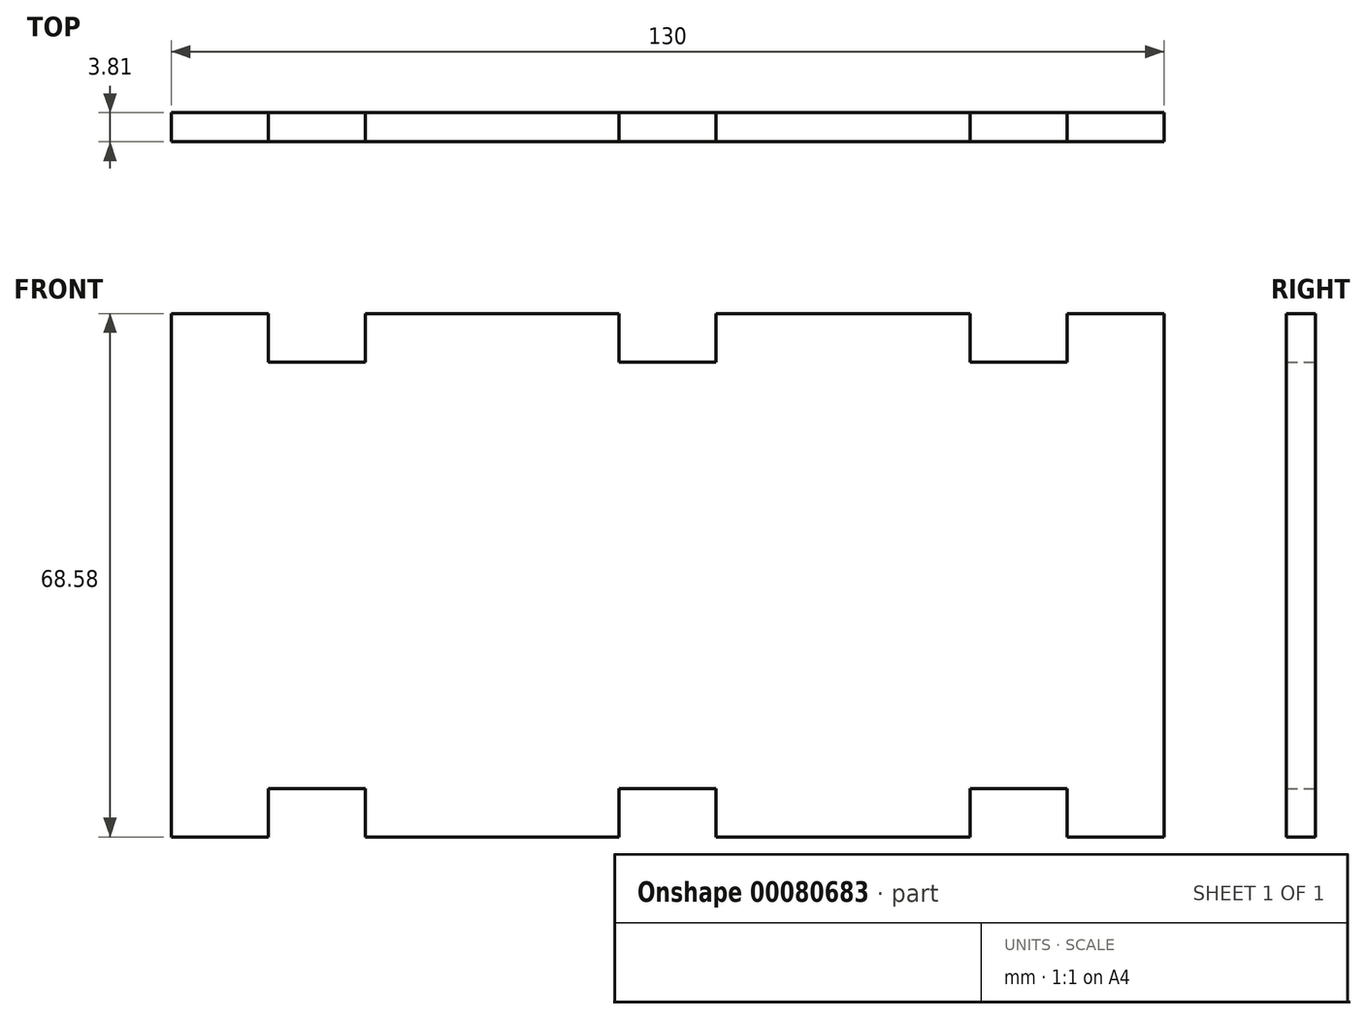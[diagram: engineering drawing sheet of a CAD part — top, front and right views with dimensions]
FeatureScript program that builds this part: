
annotation { "Feature Type Name" : "Feature", "Feature Type Description" : "" }
export const myFeature = defineFeature(function(context is Context, id is Id, definition is map)
    precondition{}
    {
        {
            var Q0;
            Q0=qCreatedBy(makeId("Front.planeOp"),FACE);
            var sketch = newSketch(context, id + "F0", { "sketchPlane" : qUnion([Q0])});
            skLineSegment(sketch, "E0.bottom", {"start": v(-65, 34.3) * mm, "end": v(-52.3, 34.3) * mm});
            skLineSegment(sketch, "E0.left", {"start": v(-65, 34.3) * mm, "end": v(-65, 0) * mm});
            skLineSegment(sketch, "E0.right", {"start": v(65, 34.3) * mm, "end": v(65, 0) * mm});
            skPoint(sketch, "E0.middle", {"position": v(0, 0) * mm});
            skLineSegment(sketch, "E1.top", {"start": v(-52.3, 27.94) * mm, "end": v(-39.6, 27.94) * mm});
            skLineSegment(sketch, "E1.left", {"start": v(-52.3, 34.3) * mm, "end": v(-52.3, 27.94) * mm});
            skLineSegment(sketch, "E1.right", {"start": v(-39.6, 34.3) * mm, "end": v(-39.6, 27.94) * mm});
            skPoint(sketch, "E1.middle", {"position": v(-45.95, 34.29) * mm});
            skLineSegment(sketch, "E2.top", {"start": v(39.6, 27.94) * mm, "end": v(52.3, 27.94) * mm});
            skLineSegment(sketch, "E2.left", {"start": v(39.6, 34.3) * mm, "end": v(39.6, 27.94) * mm});
            skLineSegment(sketch, "E2.right", {"start": v(52.3, 34.3) * mm, "end": v(52.3, 27.94) * mm});
            skPoint(sketch, "E2.middle", {"position": v(45.95, 34.3) * mm});
            skLineSegment(sketch, "E3.top", {"start": v(-6.35, 27.94) * mm, "end": v(6.35, 27.94) * mm});
            skLineSegment(sketch, "E3.left", {"start": v(-6.35, 34.3) * mm, "end": v(-6.35, 27.94) * mm});
            skLineSegment(sketch, "E3.right", {"start": v(6.35, 34.3) * mm, "end": v(6.35, 27.94) * mm});
            skPoint(sketch, "E3.middle", {"position": v(0, 34.3) * mm});
            skPoint(sketch, "E4.orphan", {"position": v(-52.3, 40.64) * mm});
            skPoint(sketch, "E5.orphan", {"position": v(-39.6, 40.64) * mm});
            skLineSegment(sketch, "E6.trimOffspring", {"start": v(-39.6, 34.3) * mm, "end": v(-6.35, 34.3) * mm});
            skPoint(sketch, "E7.orphan", {"position": v(-6.35, 40.64) * mm});
            skLineSegment(sketch, "E8.trimOffspring", {"start": v(6.35, 34.3) * mm, "end": v(39.6, 34.3) * mm});
            skPoint(sketch, "E9.orphan", {"position": v(6.35, 40.64) * mm});
            skPoint(sketch, "E2.bottom.start.orphan", {"position": v(39.6, 40.64) * mm});
            skPoint(sketch, "E10.orphan", {"position": v(52.3, 40.64) * mm});
            skPoint(sketch, "E11.orphan", {"position": v(39.6, -40.64) * mm});
            skPoint(sketch, "E12.orphan", {"position": v(52.3, -40.64) * mm});
            skPoint(sketch, "E13.orphan", {"position": v(6.35, -40.64) * mm});
            skPoint(sketch, "E14.orphan", {"position": v(-6.35, -40.64) * mm});
            skPoint(sketch, "E15.orphan", {"position": v(-39.6, -40.64) * mm});
            skPoint(sketch, "E16.orphan", {"position": v(-52.3, -40.64) * mm});
            skLineSegment(sketch, "E17.trimOffspring", {"start": v(52.3, 34.3) * mm, "end": v(65, 34.3) * mm});
            skPoint(sketch, "E18.MirrorCS.end.orphan", {"position": v(-39.6, -27.94) * mm});
            skPoint(sketch, "E18.MirrorCS.start.orphan", {"position": v(-52.3, -27.94) * mm});
            skPoint(sketch, "E0.top.start.orphan", {"position": v(-65, -34.3) * mm});
            skPoint(sketch, "E19.MirrorCS.end.orphan", {"position": v(-6.35, -27.94) * mm});
            skPoint(sketch, "E20.MirrorCS.end.orphan", {"position": v(6.35, -27.94) * mm});
            skPoint(sketch, "E21.MirrorCS.end.orphan", {"position": v(39.6, -27.94) * mm});
            skPoint(sketch, "E22.MirrorCS.end.orphan", {"position": v(52.3, -27.94) * mm});
            skPoint(sketch, "E23.orphan", {"position": v(65, -34.3) * mm});
            skLineSegment(sketch, "E24.MirrorCS", {"start": v(-65, -34.3) * mm, "end": v(-65, 0) * mm});
            skLineSegment(sketch, "E25.MirrorCS", {"start": v(-65, -34.3) * mm, "end": v(-52.3, -34.3) * mm});
            skLineSegment(sketch, "E26.MirrorCS", {"start": v(-52.3, -34.3) * mm, "end": v(-52.3, -27.94) * mm});
            skLineSegment(sketch, "E27.MirrorCS", {"start": v(-52.3, -27.94) * mm, "end": v(-39.6, -27.94) * mm});
            skLineSegment(sketch, "E28.MirrorCS", {"start": v(-39.6, -34.3) * mm, "end": v(-39.6, -27.94) * mm});
            skLineSegment(sketch, "E29.MirrorCS", {"start": v(-39.6, -34.3) * mm, "end": v(-6.35, -34.3) * mm});
            skLineSegment(sketch, "E30.MirrorCS", {"start": v(-6.35, -34.3) * mm, "end": v(-6.35, -27.94) * mm});
            skLineSegment(sketch, "E31.MirrorCS", {"start": v(-6.35, -27.94) * mm, "end": v(6.35, -27.94) * mm});
            skLineSegment(sketch, "E32.MirrorCS", {"start": v(6.35, -34.3) * mm, "end": v(39.6, -34.3) * mm});
            skLineSegment(sketch, "E33", {"start": v(6.35, -27.94) * mm, "end": v(6.35, -34.3) * mm});
            skLineSegment(sketch, "E34", {"start": v(39.6, -34.3) * mm, "end": v(39.6, -27.94) * mm});
            skLineSegment(sketch, "E35", {"start": v(52.3, -27.94) * mm, "end": v(39.6, -27.94) * mm});
            skLineSegment(sketch, "E36", {"start": v(65, -34.3) * mm, "end": v(52.3, -34.3) * mm});
            skLineSegment(sketch, "E37", {"start": v(52.3, -34.3) * mm, "end": v(52.3, -27.94) * mm});
            skLineSegment(sketch, "E38", {"start": v(65, -34.3) * mm, "end": v(65, 0) * mm});
            skSolve(sketch);
        }
        {
            var Q0;
            Q0=makeQuery(id+"F0.imprint","IMPRINT",FACE,{"disambiguationData":[TD([[makeQuery(id+"F0.imprint","IMPRINT",EDGE,{"derivedFrom":sQuery(id+"F0.wireOp",EDGE,"E0.bottom")}),-1.0]])]});
            extrude(context, id + "F1", {"entities" : qUnion([Q0]), "depth" : 3.8 * mm});
        }
    });
